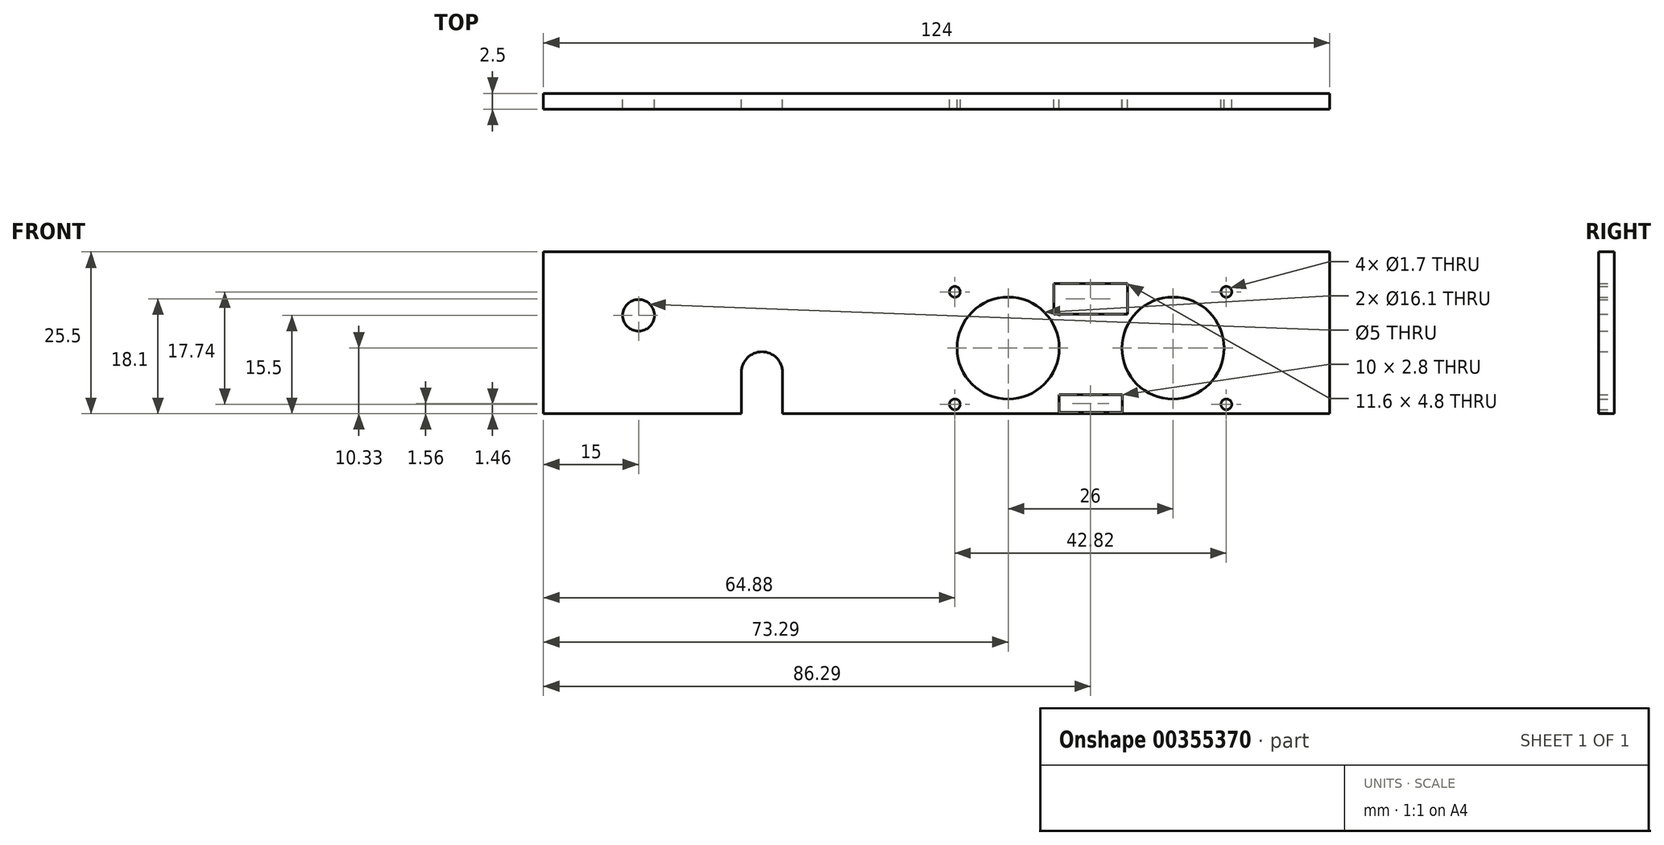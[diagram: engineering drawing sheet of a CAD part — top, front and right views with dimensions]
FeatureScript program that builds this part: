
annotation { "Feature Type Name" : "Feature", "Feature Type Description" : "" }
export const myFeature = defineFeature(function(context is Context, id is Id, definition is map)
    precondition{}
    {
        {
            var Q0;
            Q0=qCreatedBy(makeId("Front.planeOp"),FACE);
            var sketch = newSketch(context, id + "F0", { "sketchPlane" : qUnion([Q0])});
            skCircle(sketch, "E0", {"center": v(15, 36.5) * mm, "radius": 2.5 * mm});
            skLineSegment(sketch, "E1.0", {"start": v(0, 21) * mm, "end": v(0, 46.5) * mm});
            skLineSegment(sketch, "E1.1", {"start": v(0, 21) * mm, "end": v(31.21, 21) * mm});
            skLineSegment(sketch, "E1.2", {"start": v(124, 21) * mm, "end": v(124, 46.5) * mm});
            skLineSegment(sketch, "E1.3", {"start": v(0, 46.5) * mm, "end": v(124, 46.5) * mm});
            skLineSegment(sketch, "E2.bottom", {"start": v(109, 41.5) * mm, "end": v(63.58, 41.5) * mm, "construction": true});
            skLineSegment(sketch, "E2.top", {"start": v(109, 21.16) * mm, "end": v(63.58, 21.16) * mm, "construction": true});
            skLineSegment(sketch, "E2.left", {"start": v(109, 41.5) * mm, "end": v(109, 21.16) * mm, "construction": true});
            skLineSegment(sketch, "E2.right", {"start": v(63.58, 41.5) * mm, "end": v(63.58, 21.16) * mm, "construction": true});
            skLineSegment(sketch, "E3", {"start": v(86.29, 41.5) * mm, "end": v(86.29, 21.16) * mm, "construction": true});
            skLineSegment(sketch, "E4", {"start": v(63.58, 31.33) * mm, "end": v(109, 31.33) * mm, "construction": true});
            skCircle(sketch, "E5", {"center": v(99.29, 31.33) * mm, "radius": 8.05 * mm});
            skLineSegment(sketch, "E6", {"start": v(80.49, 41.5) * mm, "end": v(86.29, 41.5) * mm});
            skLineSegment(sketch, "E7", {"start": v(80.49, 41.5) * mm, "end": v(80.49, 36.7) * mm});
            skLineSegment(sketch, "E8", {"start": v(86.29, 36.7) * mm, "end": v(80.49, 36.7) * mm});
            skLineSegment(sketch, "E9", {"start": v(81.29, 23.96) * mm, "end": v(86.29, 23.96) * mm});
            skLineSegment(sketch, "E10", {"start": v(81.29, 23.96) * mm, "end": v(81.29, 21.16) * mm});
            skLineSegment(sketch, "E11", {"start": v(86.29, 21.16) * mm, "end": v(81.29, 21.16) * mm});
            skLineSegment(sketch, "E12.MirrorCS", {"start": v(86.29, 36.7) * mm, "end": v(92.09, 36.7) * mm});
            skLineSegment(sketch, "E13.MirrorCS", {"start": v(92.09, 41.5) * mm, "end": v(92.09, 36.7) * mm});
            skCircle(sketch, "E14.MirrorC", {"center": v(73.29, 31.33) * mm, "radius": 8.05 * mm});
            skLineSegment(sketch, "E15.MirrorCS", {"start": v(91.29, 23.96) * mm, "end": v(86.29, 23.96) * mm});
            skLineSegment(sketch, "E16.MirrorCS", {"start": v(91.29, 23.96) * mm, "end": v(91.29, 21.16) * mm});
            skLineSegment(sketch, "E17.MirrorCS", {"start": v(63.58, 21.16) * mm, "end": v(109, 21.16) * mm, "construction": true});
            skLineSegment(sketch, "E18", {"start": v(92.09, 41.5) * mm, "end": v(86.29, 41.5) * mm});
            skLineSegment(sketch, "E19", {"start": v(91.29, 21.16) * mm, "end": v(86.29, 21.16) * mm});
            skCircle(sketch, "E20", {"center": v(107.7, 40.2) * mm, "radius": 0.85 * mm});
            skCircle(sketch, "E21.MirrorC", {"center": v(107.7, 22.46) * mm, "radius": 0.85 * mm});
            skCircle(sketch, "E22.MirrorC", {"center": v(64.88, 40.2) * mm, "radius": 0.85 * mm});
            skCircle(sketch, "E23.MirrorC", {"center": v(64.88, 22.46) * mm, "radius": 0.85 * mm});
            skLineSegment(sketch, "E24.trimOffspring", {"start": v(37.71, 21) * mm, "end": v(124, 21) * mm});
            skLineSegment(sketch, "E25", {"start": v(31.21, 21) * mm, "end": v(31.21, 27.5) * mm});
            skLineSegment(sketch, "E26", {"start": v(37.71, 21) * mm, "end": v(37.71, 27.5) * mm});
            skArc(sketch, "E27", {"start": v(37.71, 27.5) * mm, "mid": v(34.46, 30.75) * mm, "end": v(31.21, 27.5) * mm});
            skSolve(sketch);
        }
        {
            var Q0;
            Q0=qSketchRegion(id+"F0",true);
            extrude(context, id + "F1", {"entities" : qUnion([Q0]), "depth" : 2.5 * mm});
        }
    });
